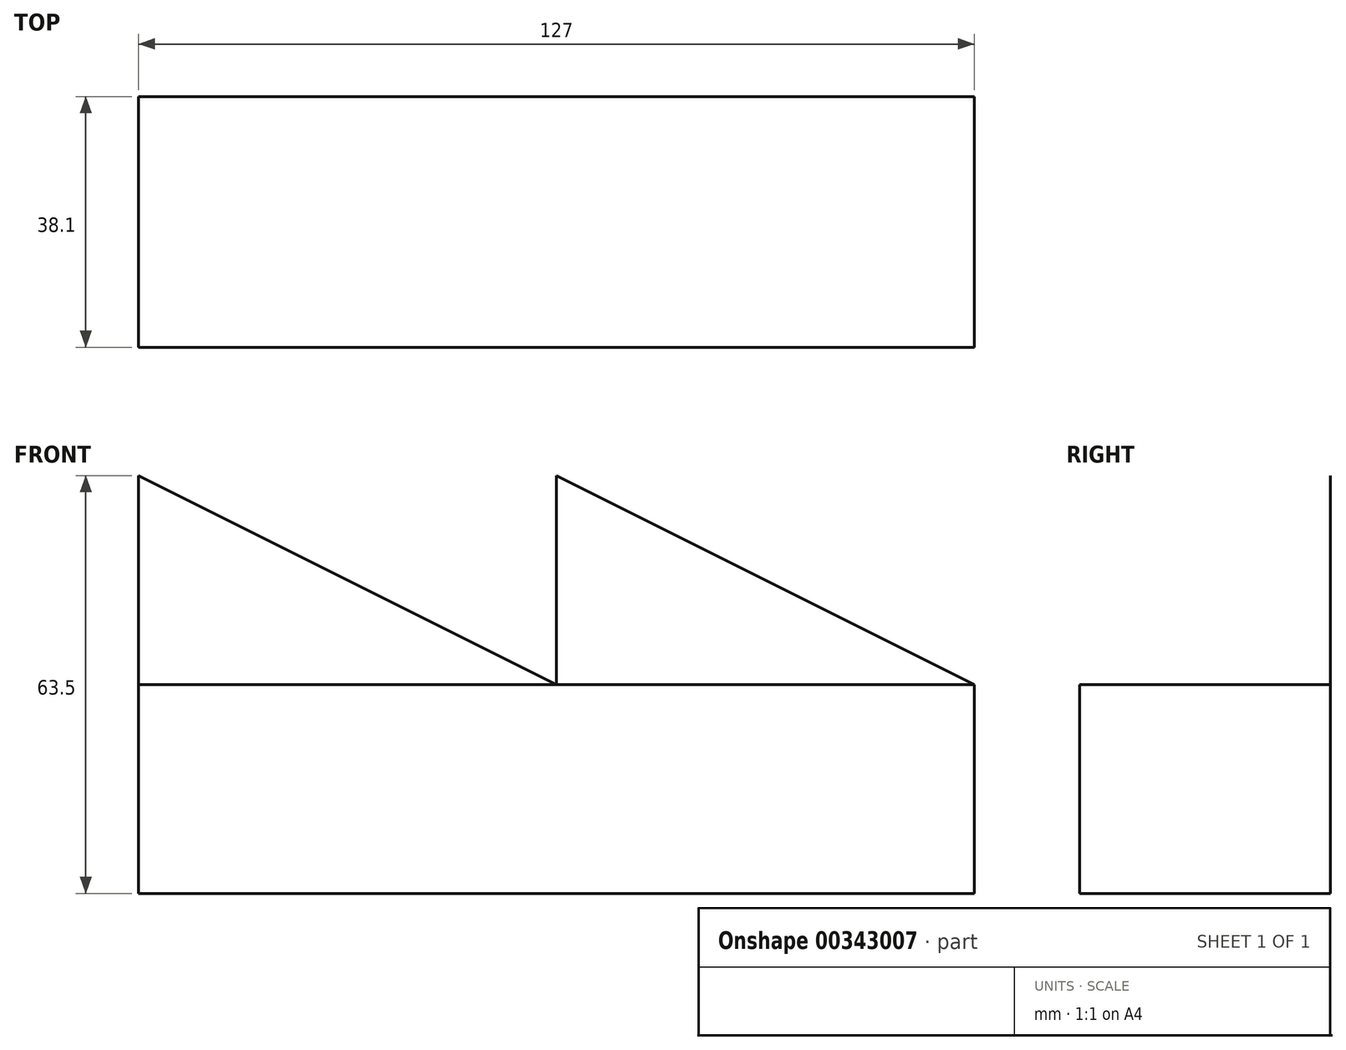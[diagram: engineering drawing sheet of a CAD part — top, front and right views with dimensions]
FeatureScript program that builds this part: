
annotation { "Feature Type Name" : "Feature", "Feature Type Description" : "" }
export const myFeature = defineFeature(function(context is Context, id is Id, definition is map)
    precondition{}
    {
        {
            var Q0;
            Q0=qCreatedBy(makeId("Front.planeOp"),FACE);
            var sketch = newSketch(context, id + "F0", { "sketchPlane" : qUnion([Q0])});
            skLineSegment(sketch, "E0.bottom", {"start": v(-63.5, -22.4) * mm, "end": v(63.5, -22.4) * mm});
            skLineSegment(sketch, "E0.top", {"start": v(-63.5, 9.34) * mm, "end": v(63.5, 9.34) * mm});
            skLineSegment(sketch, "E0.left", {"start": v(-63.5, -22.4) * mm, "end": v(-63.5, 9.34) * mm});
            skLineSegment(sketch, "E0.right", {"start": v(63.5, -22.4) * mm, "end": v(63.5, 9.34) * mm});
            skLineSegment(sketch, "E1", {"start": v(-63.5, 9.34) * mm, "end": v(-63.5, 41.1) * mm});
            skLineSegment(sketch, "E2", {"start": v(-63.5, 9.34) * mm, "end": v(0, 9.34) * mm});
            skLineSegment(sketch, "E3", {"start": v(-63.5, 41.1) * mm, "end": v(0, 9.34) * mm});
            skLineSegment(sketch, "E4", {"start": v(0, 41.1) * mm, "end": v(0, 9.34) * mm});
            skLineSegment(sketch, "E5", {"start": v(0, 41.1) * mm, "end": v(63.5, 9.34) * mm});
            skSolve(sketch);
        }
        {
            var Q0;
            Q0=makeQuery(id+"F0.imprint","IMPRINT",FACE,{"disambiguationData":[TD([[makeQuery(id+"F0.imprint","IMPRINT",EDGE,{"derivedFrom":sQuery(id+"F0.wireOp",EDGE,"E0.bottom")}),1.0]])]});
            extrude(context, id + "F1", {"entities" : qUnion([Q0]), "depth" : 38.1 * mm});
        }
        {
            var Q0;
            Q0=makeQuery(id+"F0.imprint","IMPRINT",FACE,{"disambiguationData":[TD([[makeQuery(id+"F0.imprint","IMPRINT",EDGE,{"derivedFrom":sQuery(id+"F0.wireOp",EDGE,"E1")}),-1.0]])]});
            var Q1;
            Q1=makeQuery(id+"F0.imprint","IMPRINT",FACE,{"disambiguationData":[TD([[makeQuery(id+"F0.imprint","IMPRINT",EDGE,{"derivedFrom":sQuery(id+"F0.wireOp",EDGE,"E0.top")}),1.0]])]});
            extrude(context, id + "F2", {"entities" : qUnion([Q0, Q1]), "operationType" : NewBodyOperationType.ADD, "depth" : 3 / 101.6 * mm});
        }
    });
